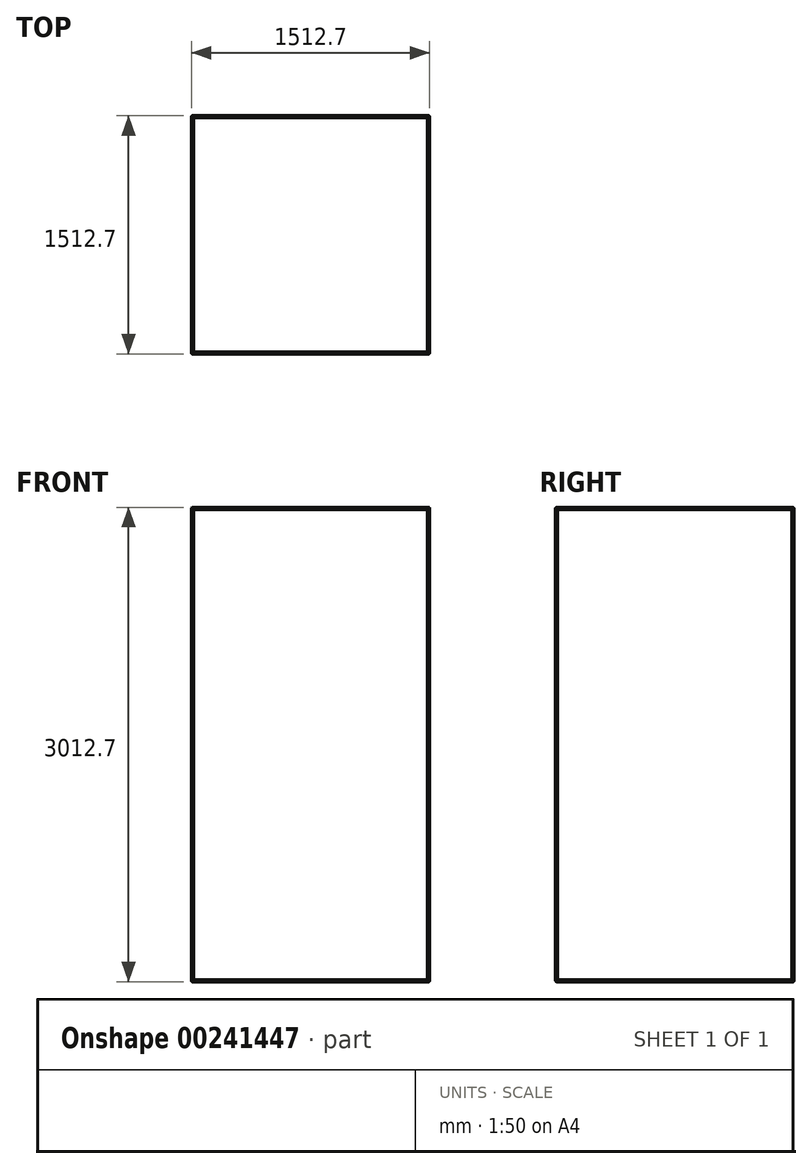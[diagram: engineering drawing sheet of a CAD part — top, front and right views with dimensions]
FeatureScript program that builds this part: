
annotation { "Feature Type Name" : "Feature", "Feature Type Description" : "" }
export const myFeature = defineFeature(function(context is Context, id is Id, definition is map)
    precondition{}
    {
        {
            var Q0;
            Q0=qCreatedBy(makeId("Right.planeOp"),FACE);
            var sketch = newSketch(context, id + "F0", { "sketchPlane" : qUnion([Q0])});
            skCircle(sketch, "E0", {"center": v(0, 0) * mm, "radius": 6.35 * mm});
            skSolve(sketch);
        }
        {
            var Q0;
            Q0 = qSketchRegion(id + "F0", true);
            extrude(context, id + "F1", {"entities" : qUnion([Q0]), "oppositeDirection" : true, "depth" : 750 * mm});
        }
        {
            var Q0;
            Q0=qCreatedBy(makeId("Front.planeOp"),FACE);
            var sketch = newSketch(context, id + "F2", { "sketchPlane" : qUnion([Q0])});
            skLineSegment(sketch, "E1", {"start": v(0, 0) * mm, "end": v(-750, 0) * mm});
            skSolve(sketch);
        }
        {
            var Q0;
            Q0=sQuery(id+"F2.wireOp",VERTEX,"E1.end");
            var Q1;
            Q1=qCreatedBy(makeId("Front.planeOp"),FACE);
            cPlane(context, id + "F3", {"entities" : qUnion([Q0, Q1]), "cplaneType" : CPlaneType.PLANE_POINT, "offset" : 25 * mm, "width" : 150 * mm, "height" : 150 * mm});
        }
        {
            var Q0;
            Q0=qCreatedBy(id+"F3.planeOp",FACE);
            var sketch = newSketch(context, id + "F4", { "sketchPlane" : qUnion([Q0])});
            skLineSegment(sketch, "E2", {"start": v(-750, 0) * mm, "end": v(-750, 3000) * mm});
            skCircle(sketch, "E3", {"center": v(-750, 0) * mm, "radius": 6.35 * mm});
            skSolve(sketch);
        }
        {
            var Q0;
            Q0=sQuery(id+"F4.wireOp",VERTEX,"E3.center");
            var Q1;
            Q1=qCreatedBy(makeId("Top.planeOp"),FACE);
            cPlane(context, id + "F5", {"entities" : qUnion([Q0, Q1]), "cplaneType" : CPlaneType.PLANE_POINT, "offset" : 25 * mm, "width" : 150 * mm, "height" : 150 * mm});
        }
        {
            var Q0;
            Q0=qCreatedBy(id+"F5.planeOp",FACE);
            var sketch = newSketch(context, id + "F6", { "sketchPlane" : qUnion([Q0])});
            skLineSegment(sketch, "E4", {"start": v(-750, 0) * mm, "end": v(-750, 375) * mm});
            skCircle(sketch, "E5", {"center": v(-750, 0) * mm, "radius": 6.35 * mm});
            skSolve(sketch);
        }
        {
            var Q0;
            Q0=makeQuery(id+"F4.imprint","IMPRINT",FACE,{"disambiguationData":[TD([[makeQuery(id+"F4.imprint","IMPRINT",EDGE,{"derivedFrom":sQuery(id+"F4.wireOp",EDGE,"E3")}),1.0]])]});
            extrude(context, id + "F7", {"entities" : qUnion([Q0]), "oppositeDirection" : true, "depth" : 750 * mm});
        }
        {
            var Q0;
            Q0 = qSketchRegion(id + "F6", true);
            extrude(context, id + "F8", {"entities" : qUnion([Q0]), "depth" : 3000 * mm});
        }
        {
            var Q0;
            Q0=qCreatedBy(id+"F3.planeOp",FACE);
            var Q1;
            Q1=sQuery(id+"F4.wireOp",VERTEX,"E2.end");
            cPlane(context, id + "F9", {"entities" : qUnion([Q0, Q1]), "cplaneType" : CPlaneType.PLANE_POINT, "offset" : 25 * mm, "width" : 150 * mm, "height" : 150 * mm});
        }
        {
            var Q0;
            Q0=qCreatedBy(id+"F9.planeOp",FACE);
            var sketch = newSketch(context, id + "F10", { "sketchPlane" : qUnion([Q0])});
            skCircle(sketch, "E6", {"center": v(-750, 3000) * mm, "radius": 6.35 * mm});
            skSolve(sketch);
        }
        {
            var Q0;
            Q0 = qSketchRegion(id + "F10", true);
            extrude(context, id + "F11", {"entities" : qUnion([Q0]), "oppositeDirection" : true, "depth" : 750 * mm});
        }
        {
            var Q0;
            Q0=sQuery(id+"F4.wireOp",VERTEX,"E2.end");
            var Q1;
            Q1=qCreatedBy(makeId("Right.planeOp"),FACE);
            cPlane(context, id + "F12", {"entities" : qUnion([Q0, Q1]), "cplaneType" : CPlaneType.PLANE_POINT, "offset" : 25 * mm, "width" : 150 * mm, "height" : 150 * mm});
        }
        {
            var Q0;
            Q0=qCreatedBy(id+"F12.planeOp",FACE);
            var sketch = newSketch(context, id + "F13", { "sketchPlane" : qUnion([Q0])});
            skCircle(sketch, "E7", {"center": v(0, 3000) * mm, "radius": 6.35 * mm});
            skSolve(sketch);
        }
        {
            var Q0;
            Q0 = qSketchRegion(id + "F13", true);
            extrude(context, id + "F14", {"entities" : qUnion([Q0]), "depth" : 750 * mm});
        }
        {
            var Q0;
            Q0=qCreatedBy(makeId("Top.planeOp"),FACE);
            var sketch = newSketch(context, id + "F15", { "sketchPlane" : qUnion([Q0])});
            skLineSegment(sketch, "E8", {"start": v(0, 0) * mm, "end": v(0, 750) * mm});
            skSolve(sketch);
        }
        {
            var Q0;
            Q0=qCreatedBy(makeId("Front.planeOp"),FACE);
            var Q1;
            Q1=sQuery(id+"F15.wireOp",VERTEX,"E8.end");
            cPlane(context, id + "F16", {"entities" : qUnion([Q0, Q1]), "cplaneType" : CPlaneType.PLANE_POINT, "offset" : 750 * mm, "oppositeDirection" : true, "width" : 150 * mm, "height" : 150 * mm});
        }
        {
            var Q0;
            Q0=makeQuery(id+"F1.opExtrude","SWEPT_BODY",BODY,{"disambiguationData":[OSD([sQuery(id+"F0.wireOp",EDGE,"E0")])]});
            var Q1;
            Q1=makeQuery(id+"F7.opExtrude","SWEPT_BODY",BODY,{"disambiguationData":[OSD([sQuery(id+"F4.wireOp",EDGE,"E3")])]});
            var Q2;
            Q2=makeQuery(id+"F8.opExtrude","SWEPT_BODY",BODY,{"disambiguationData":[OSD([sQuery(id+"F6.wireOp",EDGE,"E5")])]});
            var Q3;
            Q3=makeQuery(id+"F14.opExtrude","SWEPT_BODY",BODY,{"disambiguationData":[OSD([sQuery(id+"F13.wireOp",EDGE,"E7")])]});
            var Q4;
            Q4=makeQuery(id+"F11.opExtrude","SWEPT_BODY",BODY,{"disambiguationData":[OSD([sQuery(id+"F10.wireOp",EDGE,"E6")])]});
            var Q5;
            Q5=qCreatedBy(makeId("Right.planeOp"),FACE);
            mirror(context, id + "F17", {"entities" : qUnion([Q0, Q1, Q2, Q3, Q4]), "mirrorPlane" : qUnion([Q5])});
        }
        {
            var Q0;
            Q0=makeQuery(id+"F14.opExtrude","SWEPT_BODY",BODY,{"disambiguationData":[OSD([sQuery(id+"F13.wireOp",EDGE,"E7")])]});
            var Q1;
            Q1=makeQuery(id+"F11.opExtrude","SWEPT_BODY",BODY,{"disambiguationData":[OSD([sQuery(id+"F10.wireOp",EDGE,"E6")])]});
            var Q2;
            Q2=makeQuery(id+"F8.opExtrude","SWEPT_BODY",BODY,{"disambiguationData":[OSD([sQuery(id+"F6.wireOp",EDGE,"E5")])]});
            var Q3;
            Q3=makeQuery(id+"F17.opPattern","COPY",BODY,{"derivedFrom":makeQuery(id+"F8.opExtrude","SWEPT_BODY",BODY,{"disambiguationData":[OSD([sQuery(id+"F6.wireOp",EDGE,"E5")])]}),"instanceName":"1"});
            var Q4;
            Q4=makeQuery(id+"F17.opPattern","COPY",BODY,{"derivedFrom":makeQuery(id+"F14.opExtrude","SWEPT_BODY",BODY,{"disambiguationData":[OSD([sQuery(id+"F13.wireOp",EDGE,"E7")])]}),"instanceName":"1"});
            var Q5;
            Q5=makeQuery(id+"F17.opPattern","COPY",BODY,{"derivedFrom":makeQuery(id+"F11.opExtrude","SWEPT_BODY",BODY,{"disambiguationData":[OSD([sQuery(id+"F10.wireOp",EDGE,"E6")])]}),"instanceName":"1"});
            var Q6;
            Q6=makeQuery(id+"F17.opPattern","COPY",BODY,{"derivedFrom":makeQuery(id+"F7.opExtrude","SWEPT_BODY",BODY,{"disambiguationData":[OSD([sQuery(id+"F4.wireOp",EDGE,"E3")])]}),"instanceName":"1"});
            var Q7;
            Q7=makeQuery(id+"F17.opPattern","COPY",BODY,{"derivedFrom":makeQuery(id+"F1.opExtrude","SWEPT_BODY",BODY,{"disambiguationData":[OSD([sQuery(id+"F0.wireOp",EDGE,"E0")])]}),"instanceName":"1"});
            var Q8;
            Q8=makeQuery(id+"F1.opExtrude","SWEPT_BODY",BODY,{"disambiguationData":[OSD([sQuery(id+"F0.wireOp",EDGE,"E0")])]});
            var Q9;
            Q9=makeQuery(id+"F7.opExtrude","SWEPT_BODY",BODY,{"disambiguationData":[OSD([sQuery(id+"F4.wireOp",EDGE,"E3")])]});
            var Q10;
            Q10=qCreatedBy(id+"F16.planeOp",FACE);
            mirror(context, id + "F18", {"entities" : qUnion([Q0, Q1, Q2, Q3, Q4, Q5, Q6, Q7, Q8, Q9]), "mirrorPlane" : qUnion([Q10])});
        }
    });
